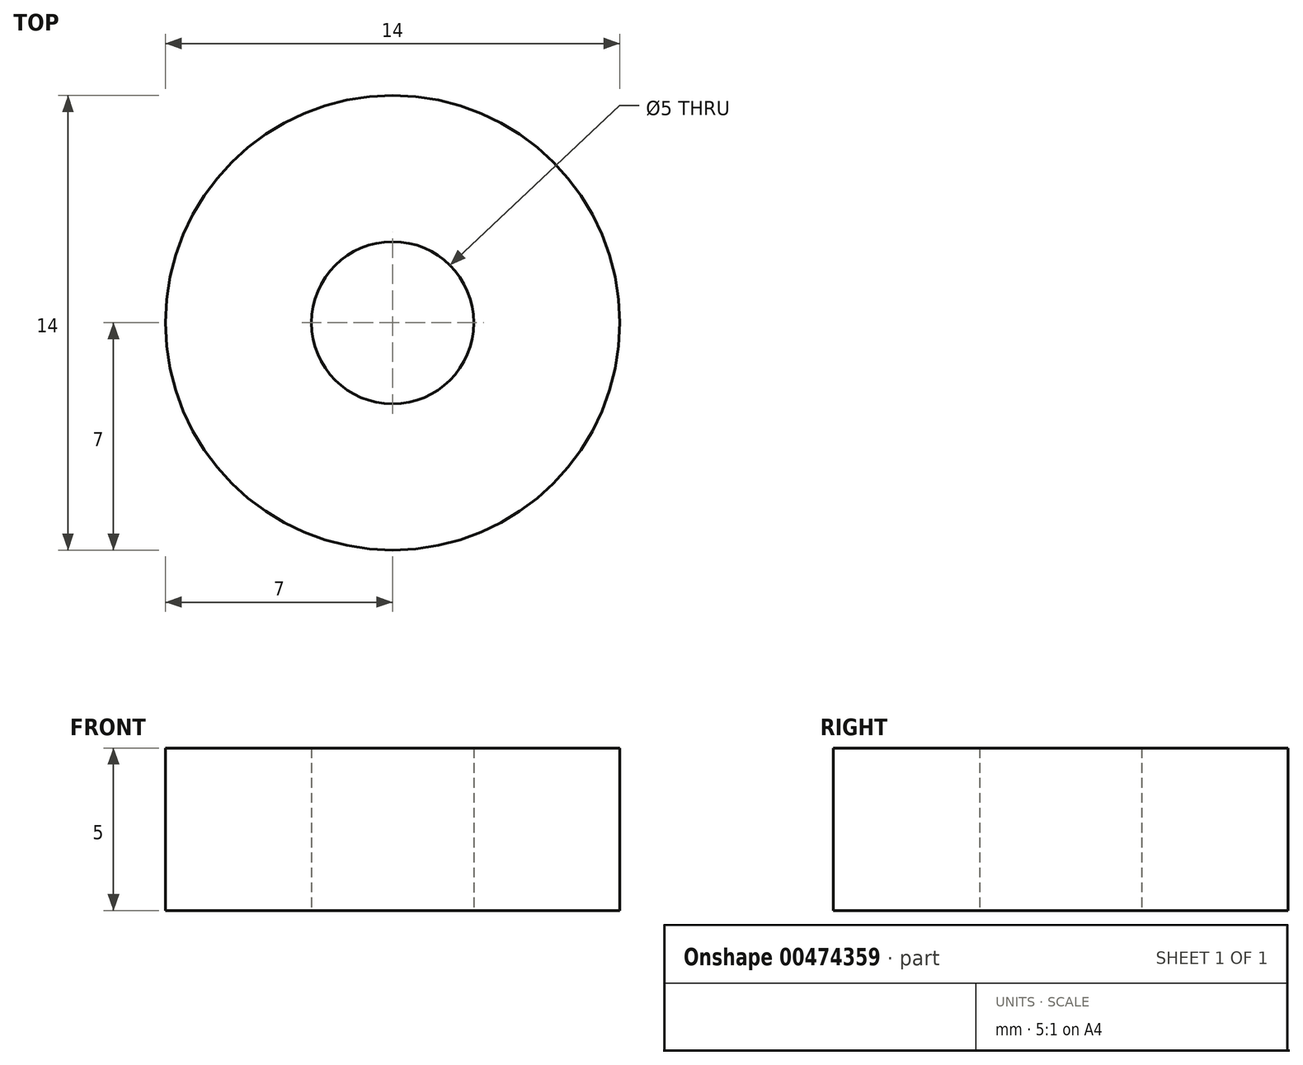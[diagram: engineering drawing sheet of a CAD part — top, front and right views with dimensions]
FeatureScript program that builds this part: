
annotation { "Feature Type Name" : "Feature", "Feature Type Description" : "" }
export const myFeature = defineFeature(function(context is Context, id is Id, definition is map)
    precondition{}
    {
        {
            var Q0;
            Q0=qCreatedBy(makeId("Top.planeOp"),FACE);
            var sketch = newSketch(context, id + "F0", { "sketchPlane" : qUnion([Q0])});
            skCircle(sketch, "E0", {"center": v(0, 0) * mm, "radius": 7 * mm});
            skCircle(sketch, "E1", {"center": v(0, 0) * mm, "radius": 2.5 * mm});
            skSolve(sketch);
        }
        {
            var Q0;
            Q0 = qSketchRegion(id + "F0", true);
            extrude(context, id + "F1", {"entities" : qUnion([Q0]), "depth" : 5 * mm});
        }
    });
